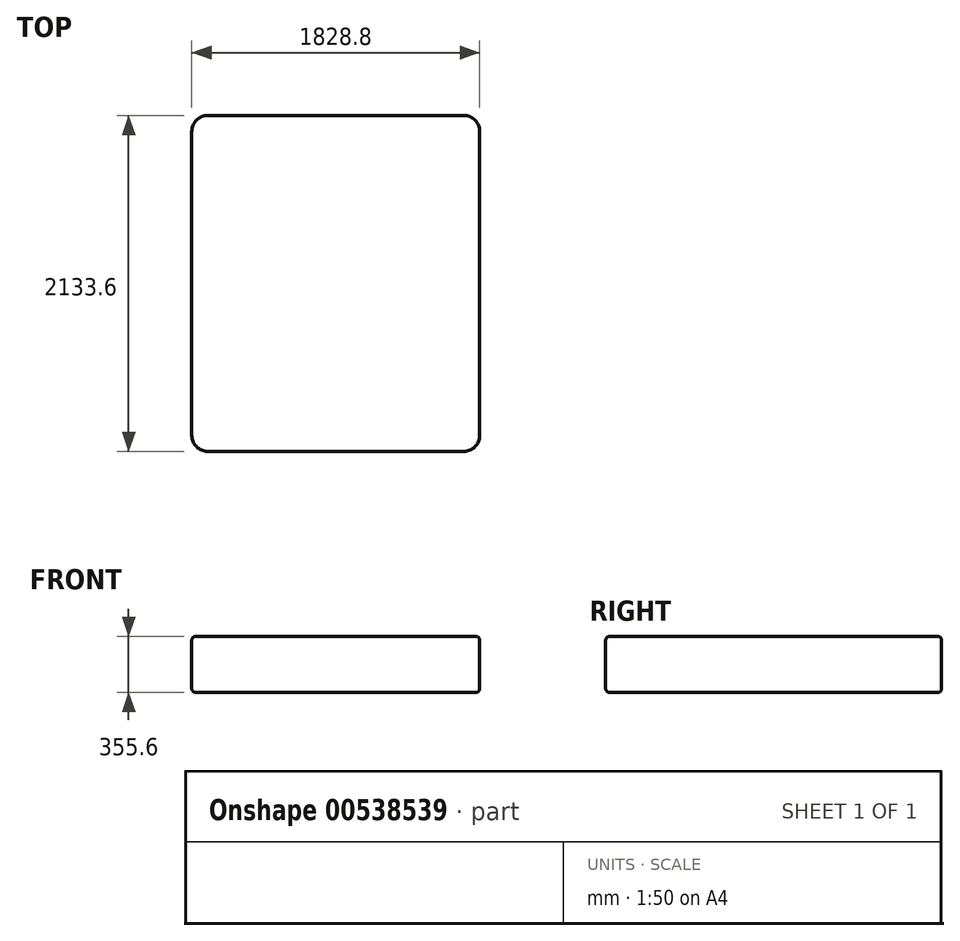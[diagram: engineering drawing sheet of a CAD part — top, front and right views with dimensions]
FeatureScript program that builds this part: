
annotation { "Feature Type Name" : "Feature", "Feature Type Description" : "" }
export const myFeature = defineFeature(function(context is Context, id is Id, definition is map)
    precondition{}
    {
        {
            var Q0;
            Q0=qCreatedBy(makeId("Top.planeOp"),FACE);
            var sketch = newSketch(context, id + "F0", { "sketchPlane" : qUnion([Q0])});
            skLineSegment(sketch, "E0.bottom", {"start": v(-914.4, 1066.8) * mm, "end": v(914.4, 1066.8) * mm});
            skLineSegment(sketch, "E0.top", {"start": v(-914.4, -1066.8) * mm, "end": v(914.4, -1066.8) * mm});
            skLineSegment(sketch, "E0.left", {"start": v(-914.4, 1066.8) * mm, "end": v(-914.4, -1066.8) * mm});
            skLineSegment(sketch, "E0.right", {"start": v(914.4, 1066.8) * mm, "end": v(914.4, -1066.8) * mm});
            skPoint(sketch, "E0.middle", {"position": v(0, 0) * mm});
            skSolve(sketch);
        }
        {
            var Q0;
            Q0=makeQuery(id+"F0.imprint","IMPRINT",FACE,{"disambiguationData":[TD([[makeQuery(id+"F0.imprint","IMPRINT",EDGE,{"derivedFrom":sQuery(id+"F0.wireOp",EDGE,"E0.bottom")}),-1.0]])]});
            extrude(context, id + "F1", {"entities" : qUnion([Q0]), "depth" : 355.6 * mm, "offsetDistance" : 25.4 * mm});
        }
        {
            var Q0;
            Q0=makeQuery(id+"F1.opExtrude","SWEPT_EDGE",EDGE,{"disambiguationData":[OSD([sQuery(id+"F0.wireOp",EDGE,"E0.top"),sQuery(id+"F0.wireOp",EDGE,"E0.left")])]});
            var Q1;
            Q1=makeQuery(id+"F1.opExtrude","SWEPT_EDGE",EDGE,{"disambiguationData":[OSD([sQuery(id+"F0.wireOp",EDGE,"E0.top"),sQuery(id+"F0.wireOp",EDGE,"E0.right")])]});
            var Q2;
            Q2=makeQuery(id+"F1.opExtrude","SWEPT_EDGE",EDGE,{"disambiguationData":[OSD([sQuery(id+"F0.wireOp",EDGE,"E0.bottom"),sQuery(id+"F0.wireOp",EDGE,"E0.right")])]});
            var Q3;
            Q3=makeQuery(id+"F1.opExtrude","SWEPT_EDGE",EDGE,{"disambiguationData":[OSD([sQuery(id+"F0.wireOp",EDGE,"E0.bottom"),sQuery(id+"F0.wireOp",EDGE,"E0.left")])]});
            fillet(context, id + "F2", {"entities" : qUnion([Q0, Q1, Q2, Q3]), "radius" : 101.6 * mm, "tangentPropagation" : true, "allowEdgeOverflow" : false});
        }
        {
            var Q0;
            {var subQ0=sQuery(id+"F0.wireOp",EDGE,"E0.right");var subQ1=sQuery(id+"F0.wireOp",EDGE,"E0.bottom");Q0=makeQuery(id+"F2.opFillet","BLEND_EDGE",EDGE,{"blendedFrom":[makeQuery(id+"F1.opExtrude","SWEPT_EDGE",EDGE,{"disambiguationData":[OSD([subQ1,subQ0])]}),makeQuery(id+"F1.opExtrude","CAP_FACE",FACE,{"disambiguationData":[OSD([subQ1,sQuery(id+"F0.wireOp",EDGE,"E0.top"),sQuery(id+"F0.wireOp",EDGE,"E0.left"),subQ0])],"isStart":false})],"blendedInto":[makeQuery(id+"F1.opExtrude","CAP_FACE",FACE,{"disambiguationData":[OSD([subQ1,sQuery(id+"F0.wireOp",EDGE,"E0.top"),sQuery(id+"F0.wireOp",EDGE,"E0.left"),subQ0])],"isStart":false})]});}
            var Q1;
            {var subQ0=sQuery(id+"F0.wireOp",EDGE,"E0.right");var subQ1=sQuery(id+"F0.wireOp",EDGE,"E0.bottom");Q1=makeQuery(id+"F2.opFillet","BLEND_EDGE",EDGE,{"blendedFrom":[makeQuery(id+"F1.opExtrude","SWEPT_EDGE",EDGE,{"disambiguationData":[OSD([subQ1,subQ0])]}),makeQuery(id+"F1.opExtrude","CAP_FACE",FACE,{"disambiguationData":[OSD([subQ1,sQuery(id+"F0.wireOp",EDGE,"E0.top"),sQuery(id+"F0.wireOp",EDGE,"E0.left"),subQ0])],"isStart":true})],"blendedInto":[makeQuery(id+"F1.opExtrude","CAP_FACE",FACE,{"disambiguationData":[OSD([subQ1,sQuery(id+"F0.wireOp",EDGE,"E0.top"),sQuery(id+"F0.wireOp",EDGE,"E0.left"),subQ0])],"isStart":true})]});}
            fillet(context, id + "F3", {"entities" : qUnion([Q0, Q1]), "radius" : 25.4 * mm, "tangentPropagation" : true, "allowEdgeOverflow" : false});
        }
    });
